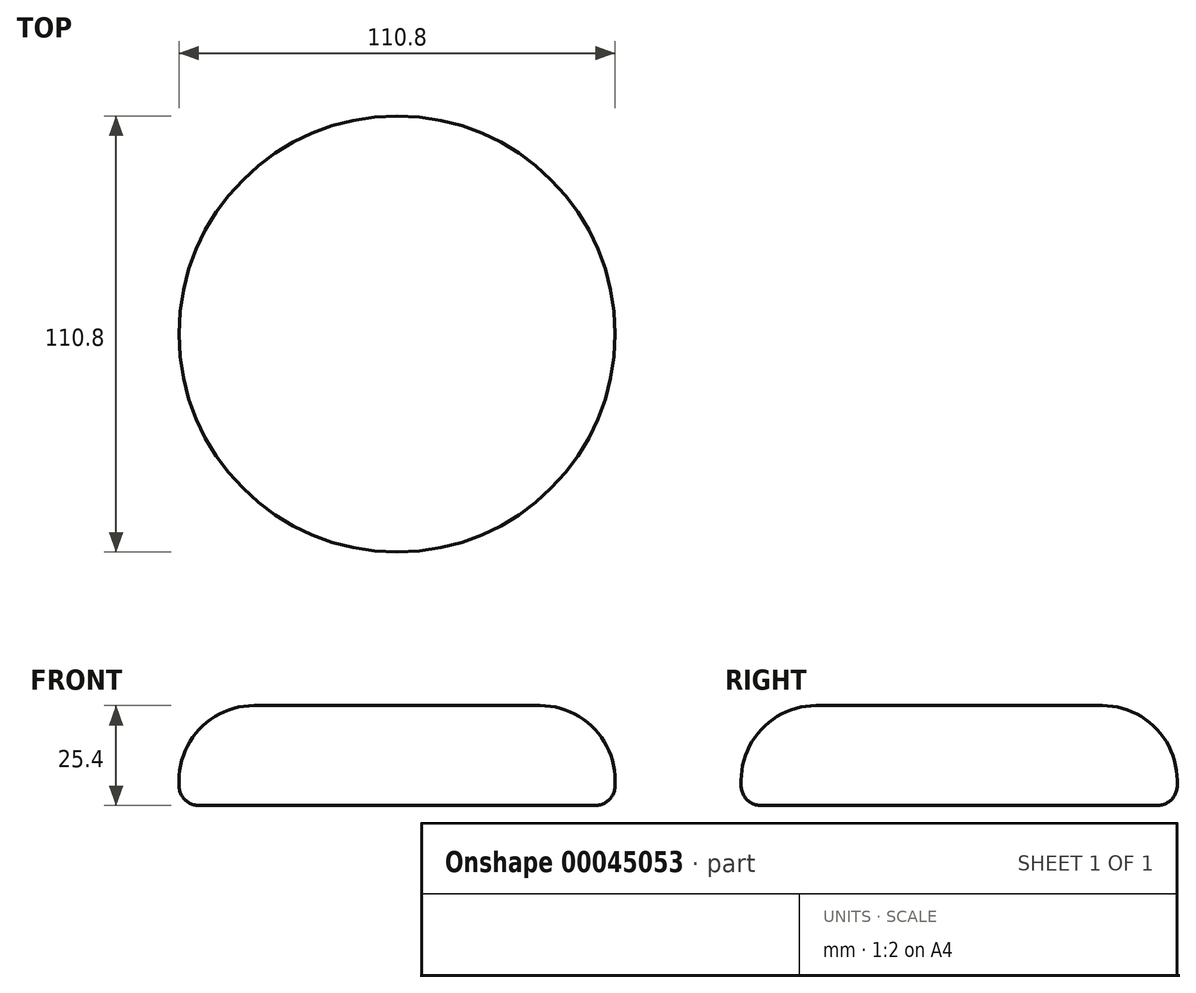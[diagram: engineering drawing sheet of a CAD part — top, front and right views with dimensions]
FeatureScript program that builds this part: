
annotation { "Feature Type Name" : "Feature", "Feature Type Description" : "" }
export const myFeature = defineFeature(function(context is Context, id is Id, definition is map)
    precondition{}
    {
        {
            var Q0;
            Q0=qCreatedBy(makeId("Top.planeOp"),FACE);
            var sketch = newSketch(context, id + "F0", { "sketchPlane" : qUnion([Q0])});
            skCircle(sketch, "E0", {"center": v(0, 0) * mm, "radius": 55.4 * mm});
            skSolve(sketch);
        }
        {
            var Q0;
            Q0 = qSketchRegion(id + "F0", true);
            extrude(context, id + "F1", {"entities" : qUnion([Q0]), "depth" : 25.4 * mm});
        }
        {
            var Q0;
            Q0=makeQuery(id+"F1.opExtrude","CAP_EDGE",EDGE,{"disambiguationData":[OSD([sQuery(id+"F0.wireOp",EDGE,"E0")])],"isStart":false});
            fillet(context, id + "F2", {"entities" : qUnion([Q0]), "radius" : 19.05 * mm, "allowEdgeOverflow" : false});
        }
        {
            var Q0;
            Q0=makeQuery(id+"F1.opExtrude","CAP_EDGE",EDGE,{"disambiguationData":[OSD([sQuery(id+"F0.wireOp",EDGE,"E0")])],"isStart":true});
            fillet(context, id + "F3", {"entities" : qUnion([Q0]), "radius" : 5.08 * mm, "tangentPropagation" : true, "allowEdgeOverflow" : false});
        }
        {
            var Q0;
            Q0=qCreatedBy(makeId("Top.planeOp"),FACE);
            cPlane(context, id + "F4", {"entities" : qUnion([Q0]), "cplaneType" : CPlaneType.OFFSET, "offset" : 6.35 * mm, "width" : 152.4 * mm, "height" : 152.4 * mm});
        }
    });
